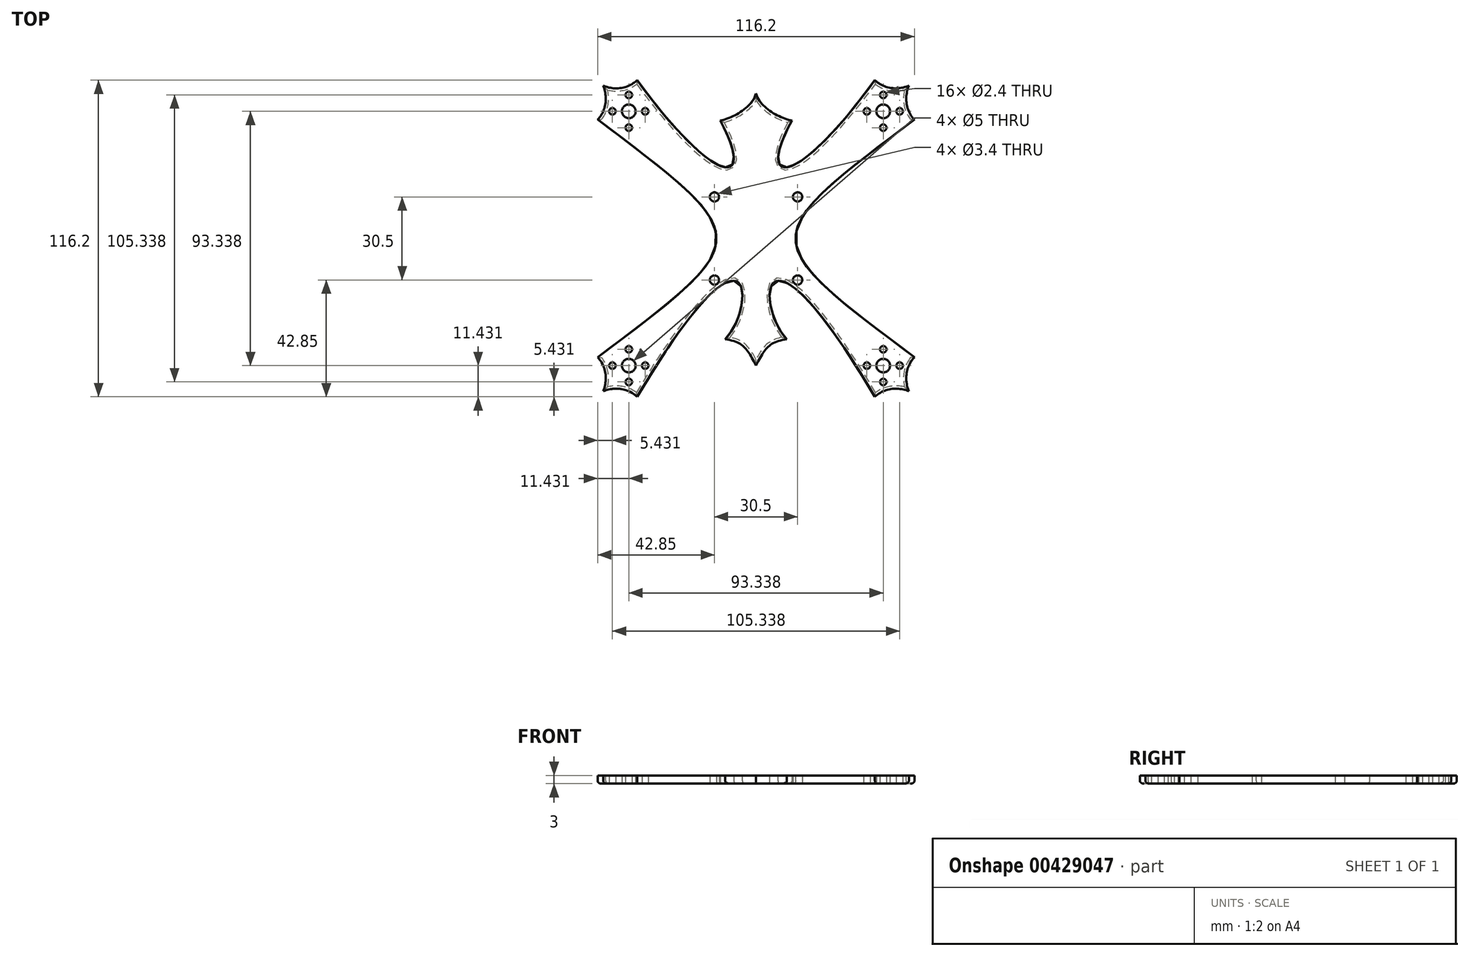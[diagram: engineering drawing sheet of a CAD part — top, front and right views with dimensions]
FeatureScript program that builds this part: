
annotation { "Feature Type Name" : "Feature", "Feature Type Description" : "" }
export const myFeature = defineFeature(function(context is Context, id is Id, definition is map)
    precondition{}
    {
        {
            var Q0;
            Q0=qCreatedBy(makeId("Top.planeOp"),FACE);
            var sketch = newSketch(context, id + "F0", { "sketchPlane" : qUnion([Q0])});
            skLineSegment(sketch, "E0.bottom", {"start": v(-46.67, 46.67) * mm, "end": v(46.67, 46.67) * mm, "construction": true});
            skLineSegment(sketch, "E0.top", {"start": v(-46.67, -46.67) * mm, "end": v(46.67, -46.67) * mm, "construction": true});
            skLineSegment(sketch, "E0.left", {"start": v(-46.67, 46.67) * mm, "end": v(-46.67, -46.67) * mm, "construction": true});
            skLineSegment(sketch, "E0.right", {"start": v(46.67, 46.67) * mm, "end": v(46.67, -46.67) * mm, "construction": true});
            skPoint(sketch, "E0.middle", {"position": v(0, 0) * mm});
            skCircle(sketch, "E1", {"center": v(-46.67, 40.67) * mm, "radius": 1.2 * mm});
            skCircle(sketch, "E2.1.0", {"center": v(-40.67, 46.67) * mm, "radius": 1.2 * mm});
            skCircle(sketch, "E2.2.0", {"center": v(-46.67, 52.67) * mm, "radius": 1.2 * mm});
            skCircle(sketch, "E2.3.0", {"center": v(-52.67, 46.67) * mm, "radius": 1.2 * mm});
            skPoint(sketch, "E2.center", {"position": v(-46.67, 46.67) * mm});
            skCircle(sketch, "E3", {"center": v(-46.67, 46.67) * mm, "radius": 2.5 * mm});
            skPoint(sketch, "E4.MirrorP", {"position": v(46.67, 46.67) * mm});
            skCircle(sketch, "E5.MirrorC", {"center": v(46.67, 40.67) * mm, "radius": 1.2 * mm});
            skCircle(sketch, "E6.MirrorC", {"center": v(40.67, 46.67) * mm, "radius": 1.2 * mm});
            skCircle(sketch, "E7.MirrorC", {"center": v(46.67, 52.67) * mm, "radius": 1.2 * mm});
            skCircle(sketch, "E8.MirrorC", {"center": v(52.67, 46.67) * mm, "radius": 1.2 * mm});
            skCircle(sketch, "E9.MirrorC", {"center": v(46.67, 46.67) * mm, "radius": 2.5 * mm});
            skPoint(sketch, "E10.MirrorP", {"position": v(-46.67, -46.67) * mm});
            skCircle(sketch, "E11.MirrorC", {"center": v(-46.67, -46.67) * mm, "radius": 2.5 * mm});
            skCircle(sketch, "E12.MirrorC", {"center": v(-52.67, -46.67) * mm, "radius": 1.2 * mm});
            skCircle(sketch, "E13.MirrorC", {"center": v(-46.67, -52.67) * mm, "radius": 1.2 * mm});
            skCircle(sketch, "E14.MirrorC", {"center": v(-40.67, -46.67) * mm, "radius": 1.2 * mm});
            skCircle(sketch, "E15.MirrorC", {"center": v(-46.67, -40.67) * mm, "radius": 1.2 * mm});
            skCircle(sketch, "E16.MirrorC", {"center": v(52.67, -46.67) * mm, "radius": 1.2 * mm});
            skCircle(sketch, "E17.MirrorC", {"center": v(46.67, -52.67) * mm, "radius": 1.2 * mm});
            skCircle(sketch, "E18.MirrorC", {"center": v(46.67, -40.67) * mm, "radius": 1.2 * mm});
            skCircle(sketch, "E19.MirrorC", {"center": v(46.67, -46.67) * mm, "radius": 2.5 * mm});
            skCircle(sketch, "E20.MirrorC", {"center": v(40.67, -46.67) * mm, "radius": 1.2 * mm});
            skLineSegment(sketch, "E21", {"start": v(-46.67, 46.67) * mm, "end": v(0, 0) * mm, "construction": true});
            skPoint(sketch, "E22.0.internal.snap0", {"position": v(0, 46.67) * mm});
            skFitSpline(sketch, "E22", {"points": [v(0, 53.21) * mm, v(-13.14, 43.25) * mm], "startDerivative": vector(-4.53, -16.25) * mm, "endDerivative": vector(-14.1, -3.4) * mm});
            skFitSpline(sketch, "E23", {"points": [v(-13.14, 43.25) * mm, v(-43.6, 58.1) * mm], "startDerivative": vector(39.42, -71.97) * mm, "endDerivative": vector(-89.9, 122.88) * mm});
            skLineSegment(sketch, "E24", {"start": v(-46.67, 46.67) * mm, "end": v(-58.9, 58.9) * mm, "construction": true});
            skFitSpline(sketch, "E25", {"points": [v(-43.6, 58.1) * mm, v(-56.07, 56.07) * mm], "startDerivative": vector(-10.44, -10.1) * mm, "endDerivative": vector(-11.48, 4.86) * mm});
            skFitSpline(sketch, "E26.MirrorCS", {"points": [v(-58.1, 43.6) * mm, v(-56.07, 56.07) * mm], "startDerivative": vector(10.1, 10.44) * mm, "endDerivative": vector(-4.86, 11.48) * mm});
            skFitSpline(sketch, "E27.MirrorCS", {"points": [v(-58.1, -43.6) * mm, v(-56.07, -56.07) * mm], "startDerivative": vector(10.1, -10.44) * mm, "endDerivative": vector(-4.86, -11.48) * mm});
            skFitSpline(sketch, "E28.MirrorCS", {"points": [v(-43.6, -58.1) * mm, v(-56.07, -56.07) * mm], "startDerivative": vector(-10.44, 10.1) * mm, "endDerivative": vector(-11.48, -4.86) * mm});
            skFitSpline(sketch, "E29", {"points": [v(-58.1, 43.6) * mm, v(-58.1, -43.6) * mm], "startDerivative": vector(174.29, -130.8) * mm, "endDerivative": vector(-174.29, -130.8) * mm});
            skFitSpline(sketch, "E30", {"points": [v(0, -46.67) * mm, v(-11.34, -36.93) * mm], "startDerivative": vector(-9.35, 18.2) * mm, "endDerivative": vector(-20.75, 3.18) * mm});
            skFitSpline(sketch, "E31", {"points": [v(-11.34, -36.93) * mm, v(-43.6, -58.1) * mm], "startDerivative": vector(34.02, 33.11) * mm, "endDerivative": vector(-130.8, -220.04) * mm});
            skFitSpline(sketch, "E32.MirrorCS", {"points": [v(13.14, 43.25) * mm, v(43.6, 58.1) * mm], "startDerivative": vector(-39.42, -71.97) * mm, "endDerivative": vector(89.9, 122.88) * mm});
            skFitSpline(sketch, "E33.MirrorCS", {"points": [v(58.1, 43.6) * mm, v(58.1, -43.6) * mm], "startDerivative": vector(-174.29, -130.8) * mm, "endDerivative": vector(174.29, -130.8) * mm});
            skFitSpline(sketch, "E34.MirrorCS", {"points": [v(58.1, 43.6) * mm, v(56.07, 56.07) * mm], "startDerivative": vector(-10.1, 10.44) * mm, "endDerivative": vector(4.86, 11.48) * mm});
            skFitSpline(sketch, "E35.MirrorCS", {"points": [v(43.6, 58.1) * mm, v(56.07, 56.07) * mm], "startDerivative": vector(10.44, -10.1) * mm, "endDerivative": vector(11.48, 4.86) * mm});
            skFitSpline(sketch, "E36.MirrorCS", {"points": [v(0, 53.21) * mm, v(13.14, 43.25) * mm], "startDerivative": vector(4.53, -16.25) * mm, "endDerivative": vector(14.1, -3.4) * mm});
            skFitSpline(sketch, "E37.MirrorCS", {"points": [v(11.34, -36.93) * mm, v(43.6, -58.1) * mm], "startDerivative": vector(-34.02, 33.11) * mm, "endDerivative": vector(130.8, -220.04) * mm});
            skFitSpline(sketch, "E38.MirrorCS", {"points": [v(0, -46.67) * mm, v(11.34, -36.93) * mm], "startDerivative": vector(9.35, 18.2) * mm, "endDerivative": vector(20.75, 3.18) * mm});
            skFitSpline(sketch, "E39.MirrorCS", {"points": [v(43.6, -58.1) * mm, v(56.07, -56.07) * mm], "startDerivative": vector(10.44, 10.1) * mm, "endDerivative": vector(11.48, -4.86) * mm});
            skFitSpline(sketch, "E40.MirrorCS", {"points": [v(58.1, -43.6) * mm, v(56.07, -56.07) * mm], "startDerivative": vector(-10.1, -10.44) * mm, "endDerivative": vector(4.86, -11.48) * mm});
            skLineSegment(sketch, "E41.bottom", {"start": v(15.25, 15.25) * mm, "end": v(-15.25, 15.25) * mm, "construction": true});
            skLineSegment(sketch, "E41.top", {"start": v(15.25, -15.25) * mm, "end": v(-15.25, -15.25) * mm, "construction": true});
            skLineSegment(sketch, "E41.left", {"start": v(15.25, 15.25) * mm, "end": v(15.25, -15.25) * mm, "construction": true});
            skLineSegment(sketch, "E41.right", {"start": v(-15.25, 15.25) * mm, "end": v(-15.25, -15.25) * mm, "construction": true});
            skCircle(sketch, "E42", {"center": v(15.25, 15.25) * mm, "radius": 1.7 * mm});
            skCircle(sketch, "E43", {"center": v(15.25, -15.25) * mm, "radius": 1.7 * mm});
            skCircle(sketch, "E44", {"center": v(-15.25, -15.25) * mm, "radius": 1.7 * mm});
            skCircle(sketch, "E45", {"center": v(-15.25, 15.25) * mm, "radius": 1.7 * mm});
            skCircle(sketch, "E46", {"center": v(-46.67, 46.67) * mm, "radius": 38.1 * mm, "construction": true});
            skLineSegment(sketch, "E47.bottom", {"start": v(-18, -18) * mm, "end": v(18, -18) * mm, "construction": true});
            skLineSegment(sketch, "E47.top", {"start": v(-18, 18) * mm, "end": v(18, 18) * mm, "construction": true});
            skLineSegment(sketch, "E47.left", {"start": v(-18, -18) * mm, "end": v(-18, 18) * mm, "construction": true});
            skLineSegment(sketch, "E47.right", {"start": v(18, -18) * mm, "end": v(18, 18) * mm, "construction": true});
            skCircle(sketch, "E48.MirrorC", {"center": v(-46.67, -46.67) * mm, "radius": 38.1 * mm, "construction": true});
            skCircle(sketch, "E49.MirrorC", {"center": v(46.67, -46.67) * mm, "radius": 38.1 * mm, "construction": true});
            skCircle(sketch, "E50.MirrorC", {"center": v(46.67, 46.67) * mm, "radius": 38.1 * mm, "construction": true});
            skSolve(sketch);
        }
        {
            var Q0;
            Q0=makeQuery(id+"F0.imprint","IMPRINT",FACE,{"disambiguationData":[TD([[makeQuery(id+"F0.imprint","IMPRINT",EDGE,{"derivedFrom":sQuery(id+"F0.wireOp",EDGE,"E1")}),-1.0]])]});
            extrude(context, id + "F1", {"entities" : qUnion([Q0]), "depth" : 3 * mm});
        }
        {
            var Q0;
            Q0=makeQuery(id+"F1.opExtrude","CAP_EDGE",EDGE,{"disambiguationData":[OSD([sQuery(id+"F0.wireOp",EDGE,"E32.MirrorCS")])],"isStart":true});
            var Q1;
            Q1=makeQuery(id+"F1.opExtrude","CAP_EDGE",EDGE,{"disambiguationData":[OSD([sQuery(id+"F0.wireOp",EDGE,"E35.MirrorCS")])],"isStart":true});
            var Q2;
            Q2=makeQuery(id+"F1.opExtrude","CAP_EDGE",EDGE,{"disambiguationData":[OSD([sQuery(id+"F0.wireOp",EDGE,"E34.MirrorCS")])],"isStart":true});
            var Q3;
            Q3=makeQuery(id+"F1.opExtrude","CAP_EDGE",EDGE,{"disambiguationData":[OSD([sQuery(id+"F0.wireOp",EDGE,"E33.MirrorCS")])],"isStart":true});
            var Q4;
            Q4=makeQuery(id+"F1.opExtrude","CAP_EDGE",EDGE,{"disambiguationData":[OSD([sQuery(id+"F0.wireOp",EDGE,"E29")])],"isStart":true});
            var Q5;
            Q5=makeQuery(id+"F1.opExtrude","CAP_EDGE",EDGE,{"disambiguationData":[OSD([sQuery(id+"F0.wireOp",EDGE,"E23")])],"isStart":true});
            var Q6;
            Q6=makeQuery(id+"F1.opExtrude","CAP_EDGE",EDGE,{"disambiguationData":[OSD([sQuery(id+"F0.wireOp",EDGE,"E22")])],"isStart":true});
            var Q7;
            Q7=makeQuery(id+"F1.opExtrude","CAP_EDGE",EDGE,{"disambiguationData":[OSD([sQuery(id+"F0.wireOp",EDGE,"E36.MirrorCS")])],"isStart":true});
            var Q8;
            Q8=makeQuery(id+"F1.opExtrude","CAP_EDGE",EDGE,{"disambiguationData":[OSD([sQuery(id+"F0.wireOp",EDGE,"E31")])],"isStart":true});
            var Q9;
            Q9=makeQuery(id+"F1.opExtrude","CAP_EDGE",EDGE,{"disambiguationData":[OSD([sQuery(id+"F0.wireOp",EDGE,"E28.MirrorCS")])],"isStart":true});
            var Q10;
            Q10=makeQuery(id+"F1.opExtrude","CAP_EDGE",EDGE,{"disambiguationData":[OSD([sQuery(id+"F0.wireOp",EDGE,"E27.MirrorCS")])],"isStart":true});
            var Q11;
            Q11=makeQuery(id+"F1.opExtrude","CAP_EDGE",EDGE,{"disambiguationData":[OSD([sQuery(id+"F0.wireOp",EDGE,"E37.MirrorCS")])],"isStart":true});
            var Q12;
            Q12=makeQuery(id+"F1.opExtrude","CAP_EDGE",EDGE,{"disambiguationData":[OSD([sQuery(id+"F0.wireOp",EDGE,"E39.MirrorCS")])],"isStart":true});
            var Q13;
            Q13=makeQuery(id+"F1.opExtrude","CAP_EDGE",EDGE,{"disambiguationData":[OSD([sQuery(id+"F0.wireOp",EDGE,"E40.MirrorCS")])],"isStart":true});
            var Q14;
            Q14=makeQuery(id+"F1.opExtrude","CAP_EDGE",EDGE,{"disambiguationData":[OSD([sQuery(id+"F0.wireOp",EDGE,"E38.MirrorCS")])],"isStart":true});
            var Q15;
            Q15=makeQuery(id+"F1.opExtrude","CAP_EDGE",EDGE,{"disambiguationData":[OSD([sQuery(id+"F0.wireOp",EDGE,"E30")])],"isStart":true});
            var Q16;
            Q16=makeQuery(id+"F1.opExtrude","CAP_EDGE",EDGE,{"disambiguationData":[OSD([sQuery(id+"F0.wireOp",EDGE,"E25")])],"isStart":true});
            var Q17;
            Q17=makeQuery(id+"F1.opExtrude","CAP_EDGE",EDGE,{"disambiguationData":[OSD([sQuery(id+"F0.wireOp",EDGE,"E26.MirrorCS")])],"isStart":true});
            fillet(context, id + "F2", {"entities" : qUnion([Q0, Q1, Q2, Q3, Q4, Q5, Q6, Q7, Q8, Q9, Q10, Q11, Q12, Q13, Q14, Q15, Q16, Q17]), "radius" : 1 * mm, "tangentPropagation" : true, "allowEdgeOverflow" : false});
        }
    });
